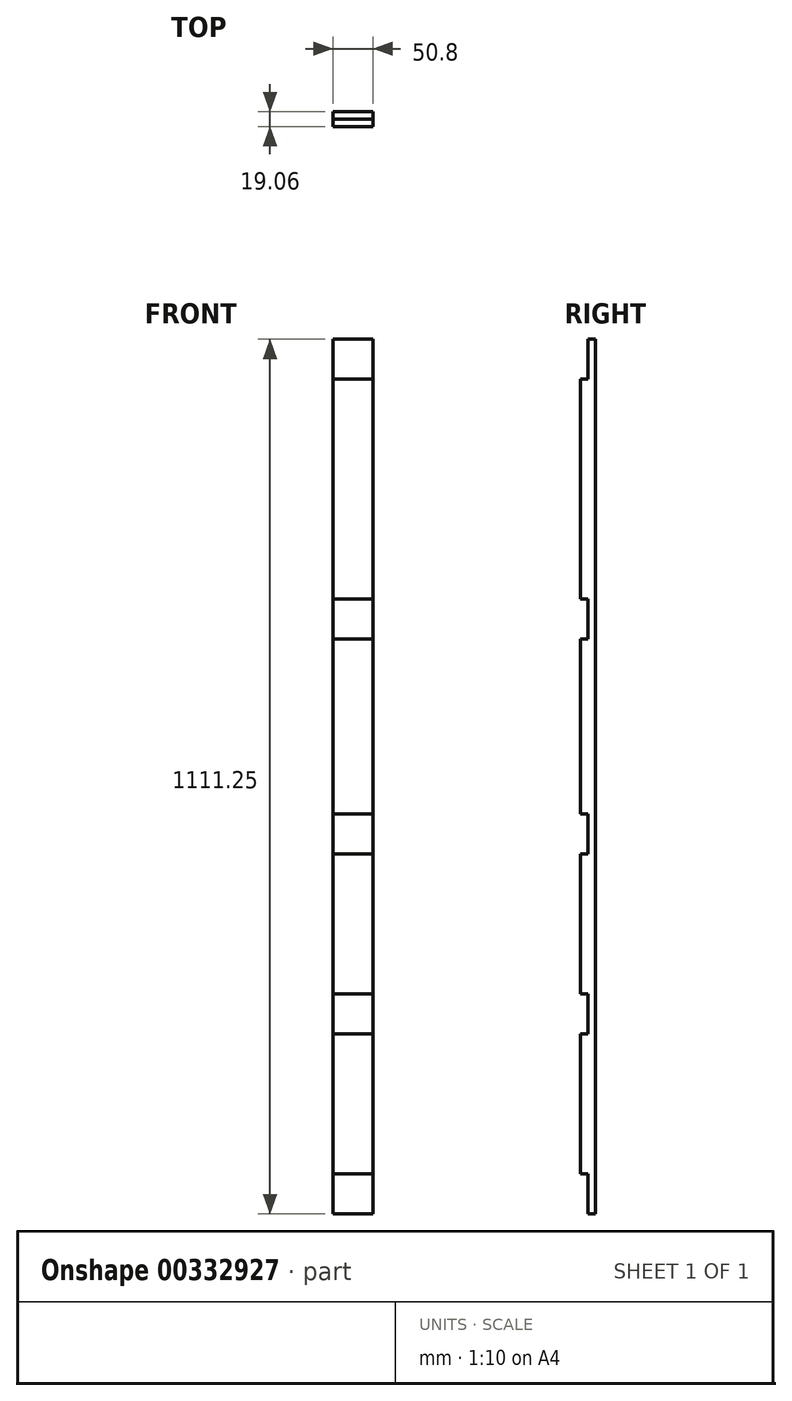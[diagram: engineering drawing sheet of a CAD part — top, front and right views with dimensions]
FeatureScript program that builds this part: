
annotation { "Feature Type Name" : "Feature", "Feature Type Description" : "" }
export const myFeature = defineFeature(function(context is Context, id is Id, definition is map)
    precondition{}
    {
        {
            var Q0;
            Q0=qCreatedBy(makeId("Top.planeOp"),FACE);
            var sketch = newSketch(context, id + "F0", { "sketchPlane" : qUnion([Q0])});
            skLineSegment(sketch, "E0.bottom", {"start": v(25.4, 9.53) * mm, "end": v(-25.4, 9.53) * mm});
            skLineSegment(sketch, "E0.top", {"start": v(25.4, -9.53) * mm, "end": v(-25.4, -9.53) * mm});
            skLineSegment(sketch, "E0.left", {"start": v(25.4, 9.53) * mm, "end": v(25.4, -9.52) * mm});
            skLineSegment(sketch, "E0.right", {"start": v(-25.4, 9.53) * mm, "end": v(-25.4, -9.53) * mm});
            skPoint(sketch, "E0.middle", {"position": v(0, 0) * mm});
            skSolve(sketch);
        }
        {
            var Q0;
            Q0=makeQuery(id+"F0.imprint","IMPRINT",FACE,{"disambiguationData":[TD([[makeQuery(id+"F0.imprint","IMPRINT",EDGE,{"derivedFrom":sQuery(id+"F0.wireOp",EDGE,"E0.bottom")}),1.0]])]});
            extrude(context, id + "F1", {"entities" : qUnion([Q0]), "depth" : 1111.25 * mm});
        }
        {
            var Q0;
            Q0=qCreatedBy(makeId("Front.planeOp"),FACE);
            var sketch = newSketch(context, id + "F2", { "sketchPlane" : qUnion([Q0])});
            skLineSegment(sketch, "E1.bottom", {"start": v(-38.77, 0) * mm, "end": v(83.66, 0) * mm});
            skLineSegment(sketch, "E1.top", {"start": v(-38.77, 50.8) * mm, "end": v(83.66, 50.8) * mm});
            skLineSegment(sketch, "E1.left", {"start": v(-38.77, 0) * mm, "end": v(-38.77, 50.8) * mm});
            skLineSegment(sketch, "E1.right", {"start": v(83.66, 0) * mm, "end": v(83.66, 50.8) * mm});
            skLineSegment(sketch, "E2.bottom", {"start": v(-44.21, 730.25) * mm, "end": v(49.65, 730.25) * mm});
            skLineSegment(sketch, "E2.top", {"start": v(-44.21, 781.05) * mm, "end": v(49.65, 781.05) * mm});
            skLineSegment(sketch, "E2.left", {"start": v(-44.21, 730.25) * mm, "end": v(-44.21, 781.05) * mm});
            skLineSegment(sketch, "E2.right", {"start": v(49.65, 730.25) * mm, "end": v(49.65, 781.05) * mm});
            skLineSegment(sketch, "E3.bottom", {"start": v(-210.36, 1060.45) * mm, "end": v(132.8, 1060.45) * mm});
            skLineSegment(sketch, "E3.top", {"start": v(-210.36, 1111.25) * mm, "end": v(132.8, 1111.25) * mm});
            skLineSegment(sketch, "E3.left", {"start": v(-210.36, 1060.45) * mm, "end": v(-210.36, 1111.25) * mm});
            skLineSegment(sketch, "E3.right", {"start": v(132.8, 1060.45) * mm, "end": v(132.8, 1111.25) * mm});
            skLineSegment(sketch, "E4.bottom", {"start": v(-116.83, 228.6) * mm, "end": v(58.93, 228.6) * mm});
            skLineSegment(sketch, "E4.top", {"start": v(-116.83, 279.4) * mm, "end": v(58.93, 279.4) * mm});
            skLineSegment(sketch, "E4.left", {"start": v(-116.83, 228.6) * mm, "end": v(-116.83, 279.4) * mm});
            skLineSegment(sketch, "E4.right", {"start": v(58.93, 228.6) * mm, "end": v(58.93, 279.4) * mm});
            skLineSegment(sketch, "E5.bottom", {"start": v(-110.63, 508) * mm, "end": v(50.66, 508) * mm});
            skLineSegment(sketch, "E5.top", {"start": v(-110.63, 457.2) * mm, "end": v(50.66, 457.2) * mm});
            skLineSegment(sketch, "E5.left", {"start": v(-110.63, 508) * mm, "end": v(-110.63, 457.2) * mm});
            skLineSegment(sketch, "E5.right", {"start": v(50.66, 508) * mm, "end": v(50.66, 457.2) * mm});
            skSolve(sketch);
        }
        {
            var Q0;
            Q0=qSketchRegion(id+"F2",true);
            extrude(context, id + "F3", {"entities" : qUnion([Q0]), "operationType" : NewBodyOperationType.REMOVE, "depth" : 25.4 * mm});
        }
        {
            var Q0;
            Q0=qCreatedBy(makeId("Front.planeOp"),FACE);
            var sketch = newSketch(context, id + "F4", { "sketchPlane" : qUnion([Q0])});
            skCircle(sketch, "E6", {"center": v(15.88, 254) * mm, "radius": 4.76 * mm});
            skCircle(sketch, "E7", {"center": v(15.87, 482.6) * mm, "radius": 4.76 * mm});
            skSolve(sketch);
        }
        {
            var Q0;
            Q0=qSketchRegion(id+"F4",true);
            extrude(context, id + "F5", {"entities" : qUnion([Q0]), "operationType" : NewBodyOperationType.REMOVE, "depth" : 25.4 * mm});
        }
    });
